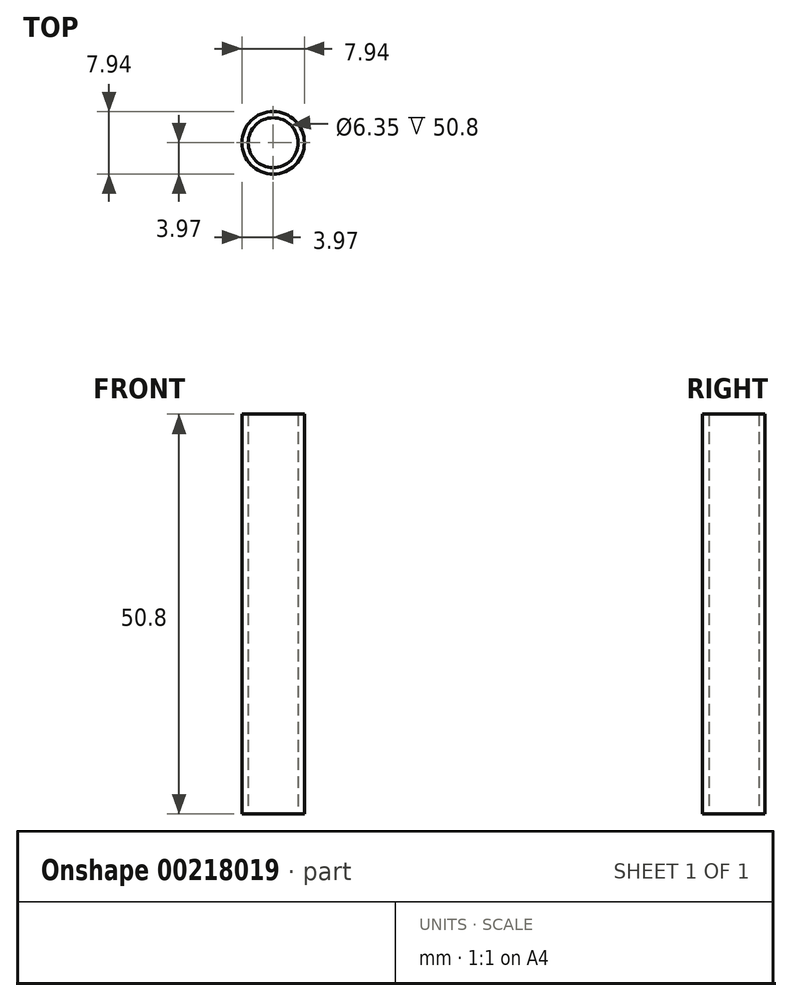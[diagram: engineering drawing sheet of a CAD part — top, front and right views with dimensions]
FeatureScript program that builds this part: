
annotation { "Feature Type Name" : "Feature", "Feature Type Description" : "" }
export const myFeature = defineFeature(function(context is Context, id is Id, definition is map)
    precondition{}
    {
        {
            var Q0;
            Q0=qCreatedBy(makeId("Top.planeOp"),FACE);
            var sketch = newSketch(context, id + "F0", { "sketchPlane" : qUnion([Q0])});
            skCircle(sketch, "E0", {"center": v(0, 0) * mm, "radius": 3.97 * mm});
            skCircle(sketch, "E1", {"center": v(0, 0) * mm, "radius": 3.18 * mm});
            skSolve(sketch);
        }
        {
            var Q0;
            Q0=qSketchRegion(id+"F0",true);
            extrude(context, id + "F1", {"entities" : qUnion([Q0]), "depth" : 50.8 * mm, "offsetDistance" : 25.4 * mm});
        }
    });
